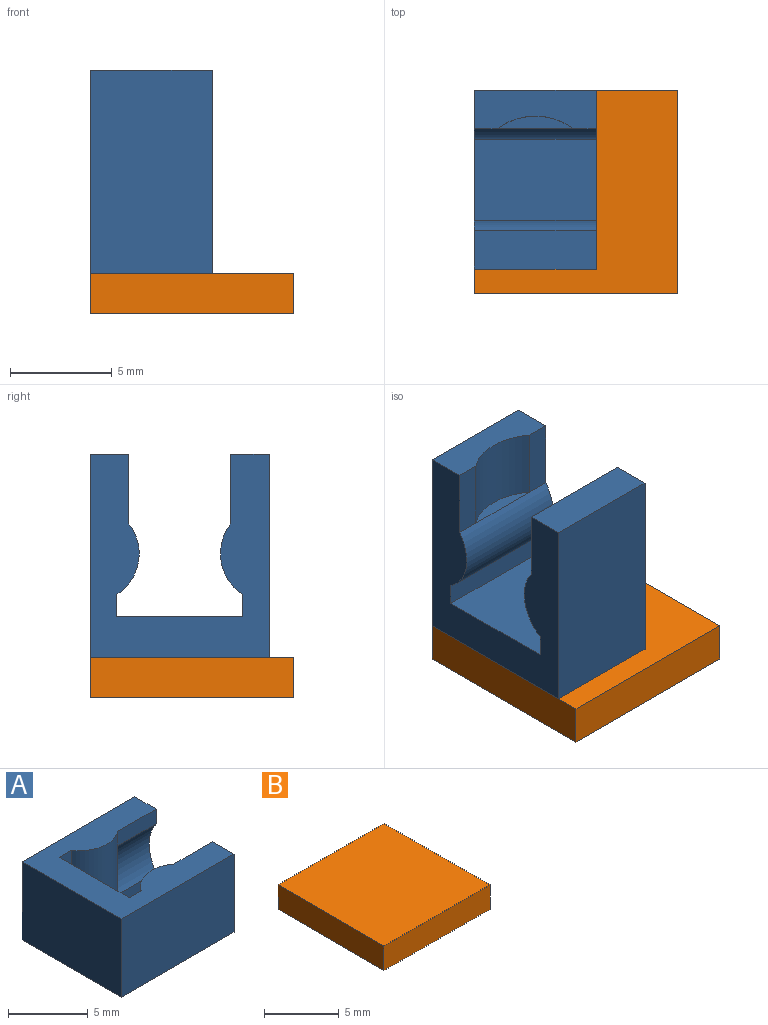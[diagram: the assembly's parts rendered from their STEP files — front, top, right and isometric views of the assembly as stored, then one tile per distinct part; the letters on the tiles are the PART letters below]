
ASSEMBLY  parts=2 mates=1
PART A: 17 faces, bbox 10x8.8x6 mm
  f0: plane 3.43x1.13mm, normal (0,-1,0), area 3.9mm2, adj f8,f10,f13,f16
  f1: plane 10x6mm, normal (0,-1,0), area 60mm2, adj f2,f12,f13,f14
  f2: plane 6x1.9mm, normal (1,0,0), area 11.4mm2, adj f1,f3,f13,f14
  f3: plane 6x3.43mm, normal (0,1,0), area 20.6mm2, adj f2,f4,f13,f14
  f4: cylinder r=2.4mm len=6mm, axis (0,0,-1), area 23.8mm2, adj f3,f5,f13,f14
  f5: plane 6x1.08mm, normal (0,1,0), area 6.5mm2, adj f4,f6,f13,f14
  f6: plane 6.2x6mm, normal (1,0,0), area 37.2mm2, adj f5,f7,f13,f14
  f7: plane 6x1.08mm, normal (0,-1,0), area 6.5mm2, adj f6,f8,f13,f14
  f8: cylinder r=2.4mm len=6mm, axis (0,0,-1), area 23.8mm2, adj f0,f7,f9,f13,f14,f15
  f9: plane 3.43x1.13mm, normal (0,-1,0), area 3.9mm2, adj f8,f10,f14,f16
  f10: plane 6x1.9mm, normal (1,0,0), area 9.8mm2, adj f0,f9,f11,f13,f14,f16
  f11: plane 10x6mm, normal (0,1,0), area 60mm2, adj f10,f12,f13,f14
  f12: plane 8.8x6mm, normal (-1,0,0), area 52.8mm2, adj f1,f11,f13,f14
  f13: plane 10x8.8mm, normal (0,0,1), area 48.4mm2, adj f0,f1,f2,f3,f4,f5,f6,f7
  f14: plane 10x8.8mm, normal (0,0,-1), area 48.4mm2, adj f1,f2,f3,f4,f5,f6,f7,f8
  f15: plane 3.75x0.63mm, normal (1,0,0), area 1.6mm2, adj f8,f16
  f16: cylinder r=3.12mm len=3.75mm, axis (1,0,0), area 13.8mm2, adj f0,f9,f10,f15
PART B: 6 faces, bbox 10x10x2 mm
  f0: plane 10x2mm, normal (0,1,0), area 20mm2, adj f1,f3,f4,f5
  f1: plane 10x2mm, normal (-1,0,0), area 20mm2, adj f0,f2,f4,f5
  f2: plane 10x2mm, normal (0,-1,0), area 20mm2, adj f1,f3,f4,f5
  f3: plane 10x2mm, normal (1,0,0), area 20mm2, adj f0,f2,f4,f5
  f4: plane 10x10mm, normal (0,0,1), area 100mm2, adj f0,f1,f2,f3
  f5: plane 10x10mm, normal (0,0,-1), area 100mm2, adj f0,f1,f2,f3
PLACE A rot(axis=(0,-1,0),90deg) t=(-0.68,-0.22,0.63)mm
PLACE B t=(-3.68,4.18,-3.37)mm
MATE fastened A.f12 <-> B.f4  axis (0,0,1) through (-3.68,4.18,-1.37)mm
